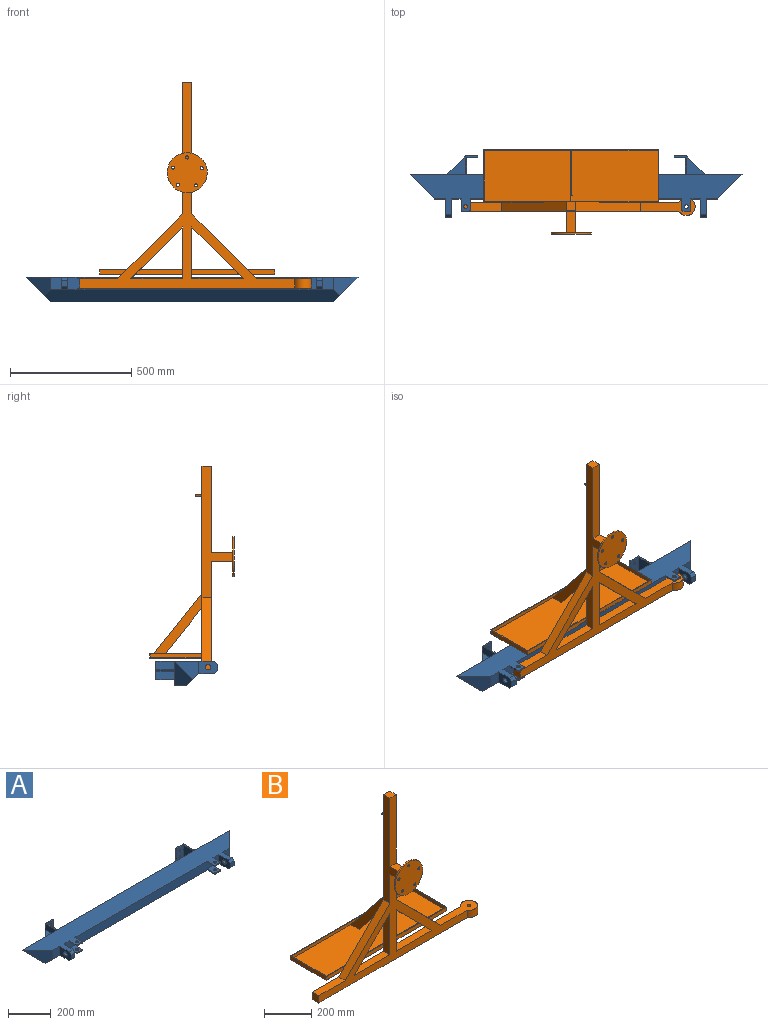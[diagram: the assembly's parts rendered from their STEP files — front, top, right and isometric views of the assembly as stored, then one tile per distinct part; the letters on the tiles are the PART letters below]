
ASSEMBLY  parts=2 mates=1
PART A: 79 faces, bbox 1371.6x254x101.6 mm
  f0: plane 76.2x34.93mm, normal (1,0,0), area 2661.3mm2, adj f1,f7,f66,f78
  f1: plane 1371.6x101.6mm, normal (0,1,0), area 127096.5mm2, adj f0,f2,f6,f7,f10,f12,f57,f58
  f2: plane 76.2x34.93mm, normal (-1,0,0), area 2661.3mm2, adj f1,f7,f61,f74
  f3: plane 50.8x45.71mm, normal (0,-1,0), area 2321.9mm2, adj f7,f8,f11,f47
  f4: plane 1026.19x50.8mm, normal (0,-1,0), area 51162.5mm2, adj f7,f8,f13,f14,f15,f17,f19,f20
  f5: plane 50.8x45.71mm, normal (0,-1,0), area 2321.9mm2, adj f7,f8,f9,f43
  f6: plane 1168.4x50.8mm, normal (0,0,-1), area 59354.7mm2, adj f1,f8,f10,f12
  f7: plane 1371.6x241.3mm, normal (0,0,1), area 137243mm2, adj f0,f1,f2,f3,f4,f5,f9,f11
  f8: plane 1219.2x50.8mm, normal (0,-0.71,-0.71), area 85765mm2, adj f3,f4,f5,f6,f9,f10,f11,f12
  f9: plane 101.6x101.6mm, normal (-0.71,-0.71,0), area 6386.8mm2, adj f5,f7,f8,f10
  f10: plane 101.6x101.6mm, normal (-0.71,0,-0.71), area 6386.8mm2, adj f1,f6,f8,f9
  f11: plane 101.6x101.6mm, normal (0.71,-0.71,0), area 6386.8mm2, adj f3,f7,f8,f12
  f12: plane 101.6x101.6mm, normal (0.71,0,-0.71), area 6386.8mm2, adj f1,f6,f8,f11
  f13: plane 45.72x6.35mm, normal (-1,0,0), area 290.3mm2, adj f4,f7,f14,f37
  f14: plane 50.8x38.1mm, normal (0,0,-1), area 1726.5mm2, adj f4,f13,f15,f16,f37,f38,f42
  f15: plane 45.72x6.35mm, normal (1,0,0), area 290.3mm2, adj f4,f7,f14,f38
  f16: plane 27.94x6.35mm, normal (0,-1,0), area 177.4mm2, adj f7,f14,f37,f38
  f17: plane 45.72x6.35mm, normal (-1,0,0), area 290.3mm2, adj f4,f18,f20,f36
  f18: plane 50.8x38.1mm, normal (0,0,-1), area 1726.5mm2, adj f8,f17,f19,f21,f35,f36,f41
  f19: plane 45.72x6.35mm, normal (1,0,0), area 290.3mm2, adj f4,f18,f20,f35
  f20: plane 50.8x38.1mm, normal (0,0,1), area 1726.5mm2, adj f4,f17,f19,f21,f35,f36,f41
  f21: plane 27.94x6.35mm, normal (0,-1,0), area 177.4mm2, adj f18,f20,f35,f36
  f22: plane 45.72x6.35mm, normal (1,0,0), area 290.3mm2, adj f4,f7,f24,f34
  f23: plane 45.72x6.35mm, normal (-1,0,0), area 290.3mm2, adj f4,f7,f24,f33
  f24: plane 50.8x38.1mm, normal (0,0,-1), area 1726.5mm2, adj f4,f22,f23,f25,f33,f34,f40
  f25: plane 27.94x6.35mm, normal (0,-1,0), area 177.4mm2, adj f7,f24,f33,f34
  f26: plane 50.8x38.1mm, normal (0,0,-1), area 1726.5mm2, adj f8,f27,f29,f30,f31,f32,f39
  f27: plane 45.72x6.35mm, normal (1,0,0), area 290.3mm2, adj f4,f26,f28,f31
  f28: plane 50.8x38.1mm, normal (0,0,1), area 1726.5mm2, adj f4,f27,f29,f30,f31,f32,f39
  f29: plane 45.72x6.35mm, normal (-1,0,0), area 290.3mm2, adj f4,f26,f28,f32
  f30: plane 27.94x6.35mm, normal (0,-1,0), area 177.4mm2, adj f26,f28,f31,f32
  f31: cylinder r=5.08mm len=6.35mm, axis (0,0,-1), area 50.7mm2, adj f26,f27,f28,f30
  f32: cylinder r=5.08mm len=6.35mm, axis (0,0,1), area 50.7mm2, adj f26,f28,f29,f30
  f33: cylinder r=5.08mm len=6.35mm, axis (0,0,1), area 50.7mm2, adj f7,f23,f24,f25
  f34: cylinder r=5.08mm len=6.35mm, axis (0,0,-1), area 50.7mm2, adj f7,f22,f24,f25
  f35: cylinder r=5.08mm len=6.35mm, axis (0,0,-1), area 50.7mm2, adj f18,f19,f20,f21
  f36: cylinder r=5.08mm len=6.35mm, axis (0,0,1), area 50.7mm2, adj f17,f18,f20,f21
  f37: cylinder r=5.08mm len=6.35mm, axis (0,0,1), area 50.7mm2, adj f7,f13,f14,f16
  f38: cylinder r=5.08mm len=6.35mm, axis (0,0,-1), area 50.7mm2, adj f7,f14,f15,f16
  f39: cylinder r=7.94mm len=15.88mm, axis (0,0,1), area 316.7mm2, adj f26,f28
  f40: cylinder r=7.94mm len=15.88mm, axis (0,0,1), area 316.7mm2, adj f7,f24
  f41: cylinder r=7.94mm len=15.88mm, axis (0,0,1), area 316.7mm2, adj f18,f20
  f42: cylinder r=7.94mm len=15.88mm, axis (0,0,1), area 316.7mm2, adj f7,f14
  f43: plane 76.2x50.8mm, normal (-1,0,0), area 3321.7mm2, adj f5,f7,f44,f46,f53,f54,f56
  f44: plane 63.5x25.4mm, normal (0,0,-1), area 1612.9mm2, adj f8,f43,f45,f54
  f45: plane 76.2x50.8mm, normal (1,0,0), area 3321.7mm2, adj f4,f7,f44,f46,f53,f54,f56
  f46: plane 25.4x25.4mm, normal (0,-1,0), area 645.2mm2, adj f43,f45,f53,f54
  f47: plane 76.2x50.8mm, normal (1,0,0), area 3321.7mm2, adj f3,f7,f49,f50,f51,f52,f55
  f48: plane 76.2x50.8mm, normal (-1,0,0), area 3321.7mm2, adj f4,f7,f49,f50,f51,f52,f55
  f49: plane 63.5x25.4mm, normal (0,0,-1), area 1612.9mm2, adj f8,f47,f48,f51
  f50: plane 25.4x25.4mm, normal (0,-1,0), area 645.2mm2, adj f47,f48,f51,f52
  f51: plane 25.4x12.7mm, normal (0,-0.71,-0.71), area 456.2mm2, adj f47,f48,f49,f50
  f52: plane 25.4x12.7mm, normal (0,-0.71,0.71), area 456.2mm2, adj f7,f47,f48,f50
  f53: plane 25.4x12.7mm, normal (0,-0.71,0.71), area 456.2mm2, adj f7,f43,f45,f46
  f54: plane 25.4x12.7mm, normal (0,-0.71,-0.71), area 456.2mm2, adj f43,f44,f45,f46
  f55: cylinder r=11.11mm len=25.4mm, axis (1,0,0), area 1773.5mm2, adj f47,f48
  f56: cylinder r=11.11mm len=25.4mm, axis (1,0,0), area 1773.5mm2, adj f43,f45
  f57: plane 76.2x34.93mm, normal (-1,0,0), area 2661.3mm2, adj f1,f61,f62,f73
  f58: plane 76.2x69.85mm, normal (1,0,0), area 5322.6mm2, adj f1,f7,f59,f62
  f59: plane 76.2x44.45mm, normal (0,-1,0), area 3133.7mm2, adj f7,f58,f60,f62,f71,f72
  f60: plane 76.2x6.35mm, normal (1,0,0), area 483.9mm2, adj f7,f59,f61,f62
  f61: plane 76.2x50.8mm, normal (0,1,0), area 3617.6mm2, adj f2,f7,f57,f60,f62,f71,f72,f75
  f62: plane 76.2x50.8mm, normal (0,0,-1), area 766.1mm2, adj f1,f57,f58,f59,f60,f61
  f63: plane 76.2x44.45mm, normal (0,-1,0), area 3133.7mm2, adj f7,f64,f67,f68,f69,f70
  f64: plane 76.2x69.85mm, normal (-1,0,0), area 5322.6mm2, adj f1,f7,f63,f68
  f65: plane 76.2x34.93mm, normal (1,0,0), area 2661.3mm2, adj f1,f66,f68,f77
  f66: plane 76.2x50.8mm, normal (0,1,0), area 3617.6mm2, adj f0,f7,f65,f67,f68,f69,f70,f76
  f67: plane 76.2x6.35mm, normal (-1,0,0), area 483.9mm2, adj f7,f63,f66,f68
  f68: plane 76.2x50.8mm, normal (0,0,-1), area 766.1mm2, adj f1,f63,f64,f65,f66,f67
  f69: cylinder r=6.35mm len=12.7mm, axis (0,1,0), area 253.4mm2, adj f63,f66
  f70: cylinder r=6.35mm len=12.7mm, axis (0,1,0), area 253.4mm2, adj f63,f66
  f71: cylinder r=6.35mm len=12.7mm, axis (0,1,0), area 253.4mm2, adj f59,f61
  f72: cylinder r=6.35mm len=12.7mm, axis (0,1,0), area 253.4mm2, adj f59,f61
  f73: plane 76.2x76.2mm, normal (0,0,-1), area 2903.2mm2, adj f1,f57,f75
  f74: plane 76.2x76.2mm, normal (0,0,1), area 2903.2mm2, adj f1,f2,f75
  f75: plane 76.2x76.2mm, normal (-0.71,0.71,0), area 684.3mm2, adj f1,f61,f73,f74
  f76: plane 76.2x76.2mm, normal (0.71,0.71,0), area 684.3mm2, adj f1,f66,f77,f78
  f77: plane 76.2x76.2mm, normal (0,0,-1), area 2903.2mm2, adj f1,f65,f76
  f78: plane 76.2x76.2mm, normal (0,0,1), area 2903.2mm2, adj f0,f1,f76
PART B: 51 faces, bbox 956.3x349.3x850.9 mm
  f0: plane 774.7x498.03mm, normal (0,1,0), area 51169.4mm2, adj f1,f13,f14,f15,f16,f17,f18,f19
  f1: plane 723.9x215.9mm, normal (0,0,1), area 5927.4mm2, adj f0,f32,f33,f34,f35,f37,f38,f39
  f2: plane 889x57.15mm, normal (0,1,0), area 36649.6mm2, adj f4,f5,f6,f7,f8,f10,f11,f13
  f3: plane 355.6x38.1mm, normal (0,-1,0), area 13548.4mm2, adj f18,f19,f20,f22
  f4: plane 214.18x38.1mm, normal (0,0,1), area 8160.4mm2, adj f2,f9,f15,f16
  f5: plane 224.72x72.73mm, normal (0,0,1), area 9813.2mm2, adj f2,f7,f9,f12,f17
  f6: plane 214.18x38.1mm, normal (0,0,1), area 8160.4mm2, adj f2,f9,f13,f14
  f7: cylinder r=36.36mm len=72.73mm, axis (0,0,1), area 7176.9mm2, adj f2,f5,f9,f10
  f8: plane 38.1x38.1mm, normal (-1,0,0), area 1451.6mm2, adj f2,f9,f10,f11
  f9: plane 889x457.2mm, normal (0,-1,0), area 75823mm2, adj f4,f5,f6,f7,f8,f10,f11,f13
  f10: plane 956.34x72.73mm, normal (0,0,-1), area 37687.8mm2, adj f2,f7,f8,f9,f12
  f11: plane 157.38x38.1mm, normal (0,0,1), area 5996.3mm2, adj f2,f8,f9,f21
  f12: cylinder r=7.94mm len=38.1mm, axis (0,0,1), area 1900.2mm2, adj f5,f10
  f13: plane 214.18x214.18mm, normal (0.71,0,-0.71), area 11540.6mm2, adj f0,f2,f6,f9,f14,f32
  f14: plane 214.18x38.1mm, normal (-1,0,0), area 8160.4mm2, adj f0,f2,f6,f9,f13,f32
  f15: plane 214.18x38.1mm, normal (1,0,0), area 8160.4mm2, adj f0,f2,f4,f9,f16,f33
  f16: plane 214.18x214.18mm, normal (-0.71,0,-0.71), area 11540.6mm2, adj f0,f2,f4,f9,f15,f33
  f17: plane 268.07x268.07mm, normal (0.71,0,0.71), area 14443.8mm2, adj f0,f2,f5,f9,f18,f39
  f18: plane 544.73x127mm, normal (1,0,0), area 24141.5mm2, adj f0,f3,f9,f17,f19,f22,f23,f26
  f19: plane 38.1x38.1mm, normal (0,0,1), area 1451.6mm2, adj f0,f3,f18,f20
  f20: plane 544.73x127mm, normal (-1,0,0), area 24141.5mm2, adj f0,f3,f9,f19,f21,f22,f23,f26
  f21: plane 268.07x268.07mm, normal (-0.71,0,0.71), area 14443.8mm2, adj f0,f2,f9,f11,f20,f34
  f22: plane 88.9x38.1mm, normal (0,0,1), area 3387.1mm2, adj f3,f18,f20,f26
  f23: plane 88.9x38.1mm, normal (0,0,-1), area 3387.1mm2, adj f9,f18,f20,f26
  f24: cylinder r=82.55mm len=165.1mm, axis (0,1,0), area 3293.6mm2, adj f25,f26
  f25: plane 165.1x165.1mm, normal (0,-1,0), area 20775mm2, adj f24,f27,f28,f29,f30,f31
  f26: plane 165.1x165.1mm, normal (0,1,0), area 19323.4mm2, adj f18,f20,f22,f23,f24,f27,f28,f29
  f27: cylinder r=6.35mm len=12.7mm, axis (0,-1,0), area 253.4mm2, adj f25,f26
  f28: cylinder r=6.35mm len=12.7mm, axis (0,-1,0), area 253.4mm2, adj f25,f26
  f29: cylinder r=6.35mm len=12.7mm, axis (0,-1,0), area 253.4mm2, adj f25,f26
  f30: cylinder r=6.35mm len=12.7mm, axis (0,-1,0), area 253.4mm2, adj f25,f26
  f31: cylinder r=6.35mm len=12.7mm, axis (0,-1,0), area 253.4mm2, adj f25,f26
  f32: plane 195.13x19.05mm, normal (0,-1,0), area 3535.9mm2, adj f1,f13,f14,f36
  f33: plane 195.13x19.05mm, normal (0,-1,0), area 3535.9mm2, adj f1,f15,f16,f36
  f34: plane 112.93x19.05mm, normal (0,-1,0), area 1969.9mm2, adj f1,f21,f36,f37
  f35: plane 215.9x19.05mm, normal (1,0,0), area 4112.9mm2, adj f1,f36,f38,f39
  f36: plane 723.9x215.9mm, normal (0,0,-1), area 156290mm2, adj f2,f32,f33,f34,f35,f37,f38,f39
  f37: plane 215.9x19.05mm, normal (-1,0,0), area 4112.9mm2, adj f1,f34,f36,f38
  f38: plane 723.9x19.05mm, normal (0,1,0), area 13790.3mm2, adj f1,f35,f36,f37
  f39: plane 112.93x19.05mm, normal (0,-1,0), area 1969.9mm2, adj f1,f17,f35,f36
  f40: plane 209.55x15.88mm, normal (1,0,0), area 3326.6mm2, adj f1,f41,f43,f44
  f41: plane 717.55x15.88mm, normal (0,1,0), area 11391.1mm2, adj f1,f40,f42,f44
  f42: plane 209.55x15.88mm, normal (-1,0,0), area 3326.6mm2, adj f1,f41,f43,f44
  f43: plane 717.55x15.88mm, normal (0,-1,0), area 11391.1mm2, adj f1,f40,f42,f44,f45
  f44: plane 717.55x209.55mm, normal (0,0,1), area 150207.7mm2, adj f40,f41,f42,f43,f46,f47,f48
  f45: plane 266x212.73mm, normal (0,0.78,0.62), area 1081.4mm2, adj f0,f43,f47,f48
  f46: plane 205x163.94mm, normal (0,-0.78,-0.62), area 833.4mm2, adj f0,f44,f47,f48
  f47: plane 266x212.73mm, normal (1,0,0), area 11488.8mm2, adj f0,f44,f45,f46
  f48: plane 266x212.73mm, normal (-1,0,0), area 11488.8mm2, adj f0,f44,f45,f46
  f49: cylinder r=3.17mm len=25.4mm, axis (0,-1,0), area 506.7mm2, adj f0,f50
  f50: plane 6.35x6.35mm, normal (0,1,0), area 31.7mm2, adj f49
PLACE A t=(-524.48,520.59,673.28)mm
PLACE B rot(axis=(0,0,1),0deg) t=(-302.71,469.79,666.93)mm
MATE planar A.f20 <-> B.f10  axis (0,0,1) through (617.26,496.07,628.83)mm
